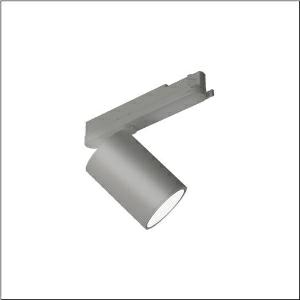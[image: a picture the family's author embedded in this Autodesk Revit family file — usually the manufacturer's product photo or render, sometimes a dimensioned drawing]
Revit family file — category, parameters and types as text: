
# Revit family: spot_31_51sf62mab4b
name_source: partatom
category: Lighting Fixtures
units: mm (PartAtom-declared; Revit-internal decimal feet)

## family parameters
Cut with Voids When Loaded = No
Host = Face
Light Source = No
Part Type = Normal
Room Calculation Point = No
Round Connector Dimension = Use Diameter
Shared = No

## types (1)
- --- (1 x LED, 4980 lm, 41.8 W, 3000K)
    Apparent Load = 42 VA
    CIE Flux Codes = 93 97 99 100 100
    Color Rendering = 90
    Color Temperature = 3000K
    Default Elevation = 1800 mm
    Description = Spot 31, directional spotlight, light control with lens, of PMMA, LED rated luminous flux: 4.790lm, light colour: 930, control gear: ECG Multilumen, with 3-phase adapter, mains connection: 220..240V, AC, 50/60Hz, of aluminium, metallic grey (RAL 9006), length: 213mm, diameter: 90mm, protection rating (complete): IP20, insulation class (complete): insulation class I (protective earthing), certification: CE, impact resistance: IK02, permissible ambient temperature for indoor applications: -20..+40°C, packaging unit: 1 piece
    Height = 175 mm
    Lamp = 1 x LED
    Lamp Light Flux = 4980 lm
    Lamp Power = 41.8 W
    Lamp count = 1
    Length = 90 mm
    Luminous efficacy = 119 lm/W
    Manufacturer = Siteco
    ModVariant = No
    Model = 51SF62MAB4B
    Mounting Place = Ceiling
    Mounting Type = Pendant
    Number of Poles = 1
    OnlyDefault = Yes
    Power Factor = 1
    Product Name = Spot 31
    Product group = directional spotlight
    ProductGroupID = 905
    Protection Class = Protection class I
    Protection Degree = IP 20
    RLX_Detail_Level = 1
    RLX_Emergency_Light_Flux = 0 lm
    RLX_Emergency_Type = 0
    RLX_Emergency_Type_DB = No
    RlxData = <blob elided: 20049 chars, md5=e6440af7>
    Socket = socket
    Standby Power = 0 W
    System Light Flux = 4980 lm
    System Power = 42 W
    Type Comments = factory setting: luminous flux: 100 % | (ON | ON | ON | ON) | 1050 mA
    Type Image = l_1273725.jpg
    URL = http://relux.com
    VarID = @adj_145985
    Voltage = 0 V
    Weight = 0.00 kg
    Width = 0 mm  [stored 0 ft]

note: [stored X ft] marks values corroborated as IEEE doubles in the binary element streams (Revit-internal decimal feet)

## geometry (parser evidence)
native form markers: Blend x4, Sweep x11
no freeform markers — native parametric forms only
